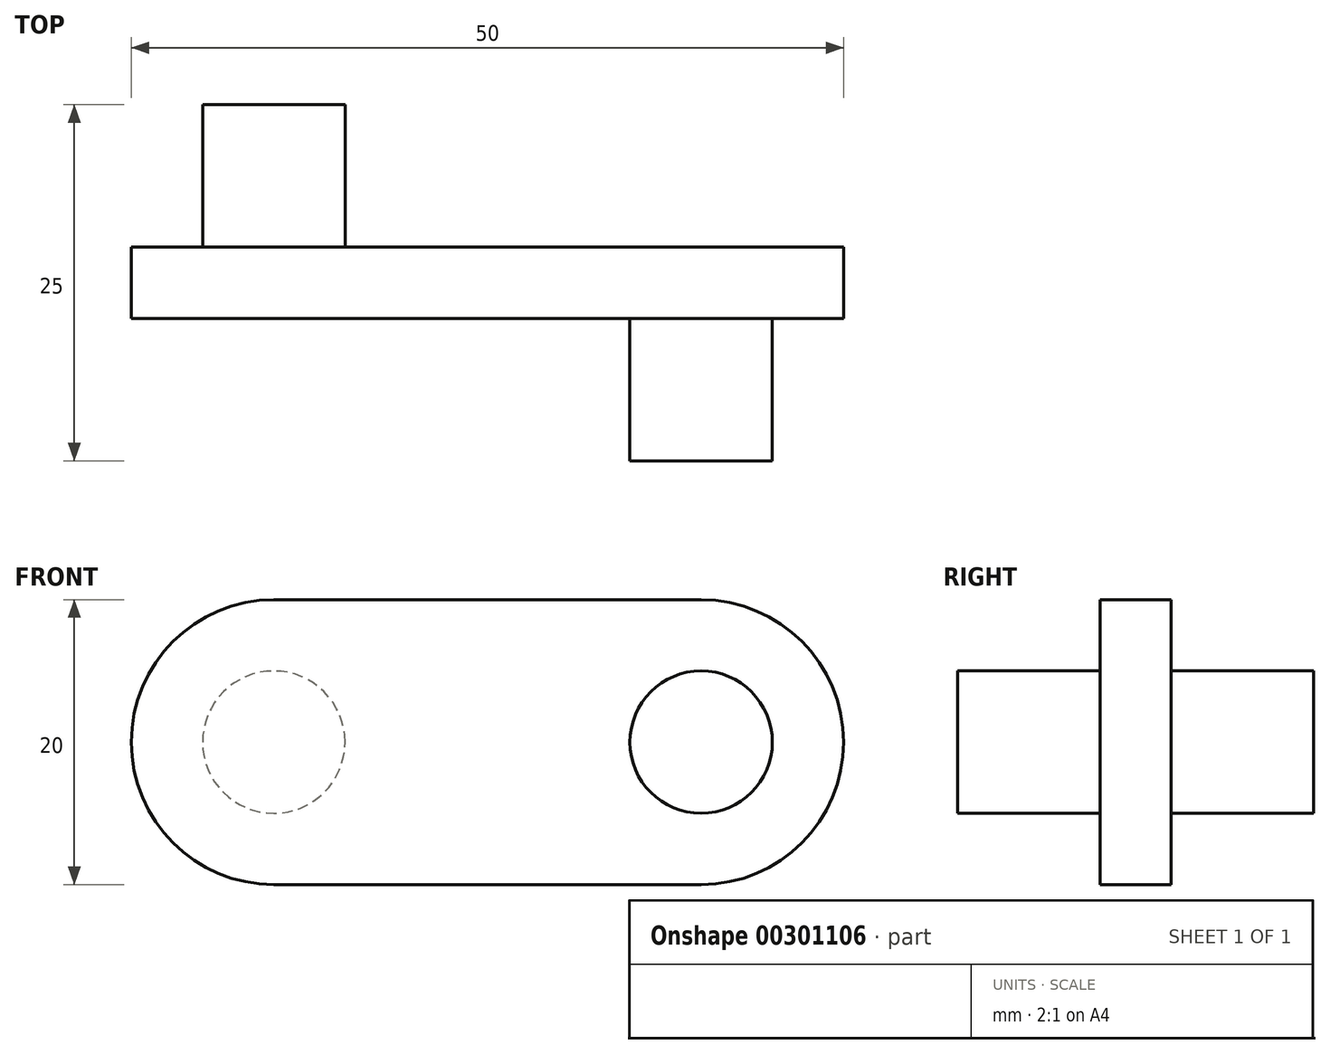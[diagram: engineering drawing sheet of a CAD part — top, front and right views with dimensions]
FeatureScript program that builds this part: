
annotation { "Feature Type Name" : "Feature", "Feature Type Description" : "" }
export const myFeature = defineFeature(function(context is Context, id is Id, definition is map)
    precondition{}
    {
        {
            var Q0;
            Q0=qCreatedBy(makeId("Front.planeOp"),FACE);
            var sketch = newSketch(context, id + "F0", { "sketchPlane" : qUnion([Q0])});
            skLineSegment(sketch, "E0.bottom", {"start": v(10, 0) * mm, "end": v(40, 0) * mm});
            skLineSegment(sketch, "E0.top", {"start": v(10, 20) * mm, "end": v(40, 20) * mm});
            skLineSegment(sketch, "E0.left", {"start": v(0, 10) * mm, "end": v(0, 10) * mm});
            skLineSegment(sketch, "E0.right", {"start": v(50, 10) * mm, "end": v(50, 10) * mm});
            skPoint(sketch, "E1.visualSharp", {"position": v(0, 20) * mm});
            skArc(sketch, "E1.filletArc", {"start": v(10, 20) * mm, "mid": v(2.93, 17.07) * mm, "end": v(0, 10) * mm});
            skPoint(sketch, "E2.visualSharp", {"position": v(0, 0) * mm});
            skArc(sketch, "E2.filletArc", {"start": v(0, 10) * mm, "mid": v(2.93, 2.93) * mm, "end": v(10, 0) * mm});
            skPoint(sketch, "E3.visualSharp", {"position": v(50, 20) * mm});
            skArc(sketch, "E3.filletArc", {"start": v(50, 10) * mm, "mid": v(47.07, 17.07) * mm, "end": v(40, 20) * mm});
            skPoint(sketch, "E4.visualSharp", {"position": v(50, 0) * mm});
            skArc(sketch, "E4.filletArc", {"start": v(40, 0) * mm, "mid": v(47.07, 2.93) * mm, "end": v(50, 10) * mm});
            skSolve(sketch);
        }
        {
            var Q0;
            Q0 = qSketchRegion(id + "F0", true);
            extrude(context, id + "F1", {"entities" : qUnion([Q0]), "depth" : 5 * mm});
        }
        {
            var Q0;
            Q0=makeQuery(id+"F1.opExtrude","CAP_FACE",FACE,{"disambiguationData":[OSD([sQuery(id+"F0.wireOp",EDGE,"E0.bottom"),sQuery(id+"F0.wireOp",EDGE,"E0.top"),sQuery(id+"F0.wireOp",EDGE,"E1.filletArc"),sQuery(id+"F0.wireOp",EDGE,"E2.filletArc"),sQuery(id+"F0.wireOp",EDGE,"E3.filletArc"),sQuery(id+"F0.wireOp",EDGE,"E4.filletArc")])],"isStart":false});
            var sketch = newSketch(context, id + "F2", { "sketchPlane" : qUnion([Q0])});
            skCircle(sketch, "E5", {"center": v(40, 10) * mm, "radius": 5 * mm});
            skSolve(sketch);
        }
        {
            var Q0;
            Q0=makeQuery(id+"F2.imprint","IMPRINT",FACE,{"disambiguationData":[TD([[makeQuery(id+"F2.imprint","IMPRINT",EDGE,{"derivedFrom":sQuery(id+"F2.wireOp",EDGE,"E5")}),1.0]])]});
            extrude(context, id + "F3", {"entities" : qUnion([Q0]), "operationType" : NewBodyOperationType.ADD, "depth" : 10 * mm});
        }
        {
            var Q0;
            Q0=makeQuery(id+"F1.opExtrude","CAP_FACE",FACE,{"disambiguationData":[OSD([sQuery(id+"F0.wireOp",EDGE,"E0.bottom"),sQuery(id+"F0.wireOp",EDGE,"E0.top"),sQuery(id+"F0.wireOp",EDGE,"E1.filletArc"),sQuery(id+"F0.wireOp",EDGE,"E2.filletArc"),sQuery(id+"F0.wireOp",EDGE,"E3.filletArc"),sQuery(id+"F0.wireOp",EDGE,"E4.filletArc")])],"isStart":true});
            var sketch = newSketch(context, id + "F4", { "sketchPlane" : qUnion([Q0])});
            skCircle(sketch, "E6", {"center": v(-10, 10) * mm, "radius": 5 * mm});
            skSolve(sketch);
        }
        {
            var Q0;
            Q0 = qSketchRegion(id + "F4", true);
            extrude(context, id + "F5", {"entities" : qUnion([Q0]), "operationType" : NewBodyOperationType.ADD, "depth" : 10 * mm});
        }
    });
